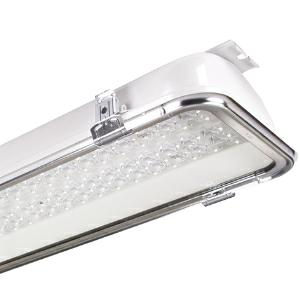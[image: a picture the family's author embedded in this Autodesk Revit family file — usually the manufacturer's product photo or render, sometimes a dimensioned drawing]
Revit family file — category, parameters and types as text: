
# Revit family: 3f_filippi_-_beta_235_76_vt_ampio_3f_filippi_-_52772_-_beta_235_led_761x60_ampio_vt_l1565
name_source: partatom
category: Lighting Fixtures
units: mm (PartAtom-declared; Revit-internal decimal feet)

## family parameters
Cut with Voids When Loaded = No
Host = Face
Light Source = No
Part Type = Normal
Room Calculation Point = No
Round Connector Dimension = Use Diameter
Shared = No

## types (1)
- 3F Filippi - Beta 235 76 VT Ampio (1 x LED, 10460 lm, 65 W, 4000 K)
    Apparent Load = 65 VA
    Approval mark = CE
    CIE Flux Codes = 56 92 99 100 100
    Color Rendering = 80
    Color Temperature = 4000 K
    Control Gear = Electronic ballast
    Default Elevation = 1800 mm
    Description = ILLUMINOTECHNICAL
Luminous efficiency 100% (DLOR 100%, ULOR 0%).
Initial luminous flux of the luminaire 10460 lm.
Wide symmetric distribution.
Installation Interdistance Transv.D = 1.19 x hu - Long.D = 1.18 x hu.
Tabular UGR (CIE 117 - 4H-8H; S=0.25H; 70/50/20): RUG 20.3 - 21.9.
Beam angle: 99° - 105°.
Luminous efficacy 161 lm/W.
Lifetime (L93/B10): 30000 h. (tq+25°C)
Lifetime (L90/B10): 50000 h. (tq+25°C)
Lifetime (L85/B10): 80000 h. (tq+25°C)
Lifetime (L80/B10): 100000 h. (tq+25°C)
Lifetime (L85/B10): 50000 h. (tq+45°C)
Sudden decreased luminous flux after 50000 hours: 0% (C0).
Photobiological safety in compliance with IEC/TR 62778: RG0 risk exempt, (IEC 62471).
In compliance with IEC/EN 62722-2-1 - IEC/EN 62717 standards.

SOURCE
Linear LED module 60W/840.
Energy efficiency class (UE 2019/2020 - UE 2019/2015): C.
CIE 13.3 Colour rendering index: CRI >80 (R9 <50%).
IES TM-30 Fidelity Index: Rf = 84 Rg = 95.
CCT nominal colour temperature 4000 K.
Colour initial tolerance (MacAdam): SDCM 3.

MECHANICAL
Single-piece housing in pressed steel, powder-coated in white epoxy-polyester.
VT transparent glass, non-combustible, single-piece perimeter frame in galvanised steel.
Ecologic anti-aging injected sealing gasket.
Oversized gear-tray reflector unit in highly reflective white painted hot-galvanised steel.
Methacrylate (PMMA) lenses with external flat surface.
Galvanised steel snap-lock clips for diffuser mounting (safety n° 4 per fixture).
Luminaire with limited surface temperature. - D - (EN 60598-2-24)
Dimensions: 1565x235 mm, height 105 mm. Weight 11.255 kg.
IP66 protection degree.
Mechanical strength to impacts IK09 (10 joule).
Glow-wire test resistance 960°C.

ELECTRICAL
Halogen Free electronic wiring 230V-50/60Hz, power factor 0.95, THD <25%, constant output current, class I, 1 driver.
Power of the luminaire 65 W.
ENEC - CE.
Flicker: <4%.
Luminaire compliant with EN 60598-2-22 for power supply from a centralised emergency system CPSS (Central Power Supply System), not incorporated in the luminaire - high risk areas excluded. The default power and flux are 100% in AC and 100% in DC.
Ambient temperature from -20°C to +45°C.
Temperature class T6 max 85°C.
Quick connection via M20 3P connector with 9-13 mm tightening range.
Relative humidity UR: <85%.

INSTALLATION
Ceiling / Suspended / Wall.
All accessories dedicated to this product are available on the Catalog and on our website www.3F-Filippi.com.

APPLICATIONS
Dry, dusty indoor environments, subject to occasional water splashes.
Industrial environments, warehouses, environments where security locks are required on all clips, e.g. prisons (on request).
Environments in which it is necessary a total protection against falling fragments (eg environments with foodstuffs or machines with moving parts or with extreme temperature changes), use luminaires with laminated glass.
Tempered glass is not immune to falling fragments from harmless and caused by shocks or exceptionally derived from the tempering process.

WARNING
Fixture not suitable for cold stores with an ambient temperature <0°C and/or relative humidity >85%.
Luminaire designed for disposal/recycling at end-of-life.
Replaceable (LED only) light source by a professional. Replaceable control gear by a professional.
    Height = 105 mm
    Lamp = 1 x LED
    Lamp Light Flux = 10460 lm
    Lamp Power = 65 W
    Lamp count = 1
    Length = 1565 mm
    Lifetime = 50000 h
    Luminous efficacy = 161 lm/W
    Manufacturer = 3F Filippi
    ModVariant = No
    Model = 3F Filippi - 52772 - Beta 235 LED 761x60 AMPIO VT L1565
    Mounting Place = Ceiling
    Mounting Type = Pendant
    Number of Poles = 1
    OnlyDefault = Yes
    Power Factor = 1
    Product Name = 3F Filippi - Beta 235 76 VT Ampio
    Product group = pendant luminaire
    ProductGroupID = 9
    Protection Class = Protection class I
    Protection Degree = IP 66
    RLX_Detail_Level = 1
    RLX_Emergency_Light_Flux = 0 lm
    RLX_Emergency_Type = 0
    RLX_Emergency_Type_DB = No
    RlxData = <blob elided: 88029 chars, md5=24228dcd>
    Socket = socket
    Standby Power = 0 W
    System Light Flux = 10460 lm
    System Power = 65 W
    Type Comments = Product without accessories
    Type Image = 3ffilippi_52772.jpg
    URL = http://relux.com
    VarID = ---
    Voltage = 0 V
    Weight = 0.00 kg
    Width = 235 mm

## geometry (parser evidence)
native form markers: Blend x4, Sweep x11
no freeform markers — native parametric forms only
